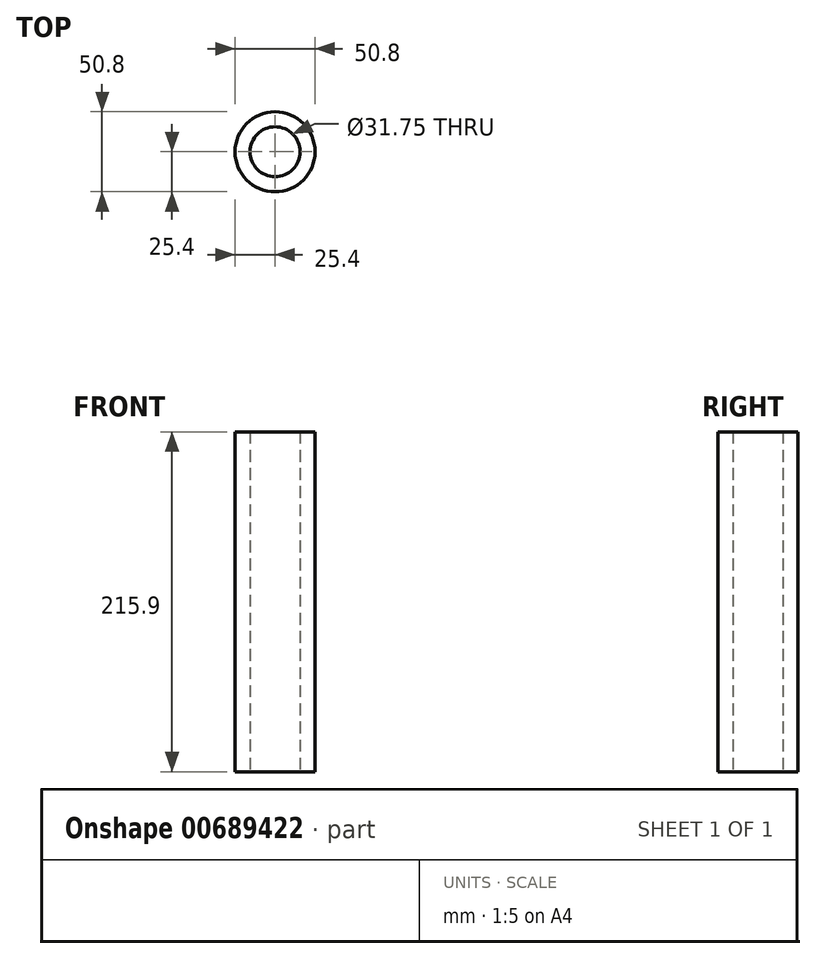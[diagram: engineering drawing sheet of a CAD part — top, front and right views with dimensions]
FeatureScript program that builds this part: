
annotation { "Feature Type Name" : "Feature", "Feature Type Description" : "" }
export const myFeature = defineFeature(function(context is Context, id is Id, definition is map)
    precondition{}
    {
        {
            var Q0;
            Q0=qCreatedBy(makeId("Top.planeOp"),FACE);
            var sketch = newSketch(context, id + "F0", { "sketchPlane" : qUnion([Q0])});
            skCircle(sketch, "E0", {"center": v(0, 0) * mm, "radius": 25.4 * mm});
            skCircle(sketch, "E1", {"center": v(0, 0) * mm, "radius": 15.88 * mm});
            skSolve(sketch);
        }
        {
            var Q0;
            Q0=makeQuery(id+"F0.imprint","IMPRINT",FACE,{"disambiguationData":[TD([[makeQuery(id+"F0.imprint","IMPRINT",EDGE,{"derivedFrom":sQuery(id+"F0.wireOp",EDGE,"E0")}),1.0]])]});
            extrude(context, id + "F1", {"entities" : qUnion([Q0]), "depth" : 215.9 * mm, "offsetDistance" : 25.4 * mm});
        }
    });
